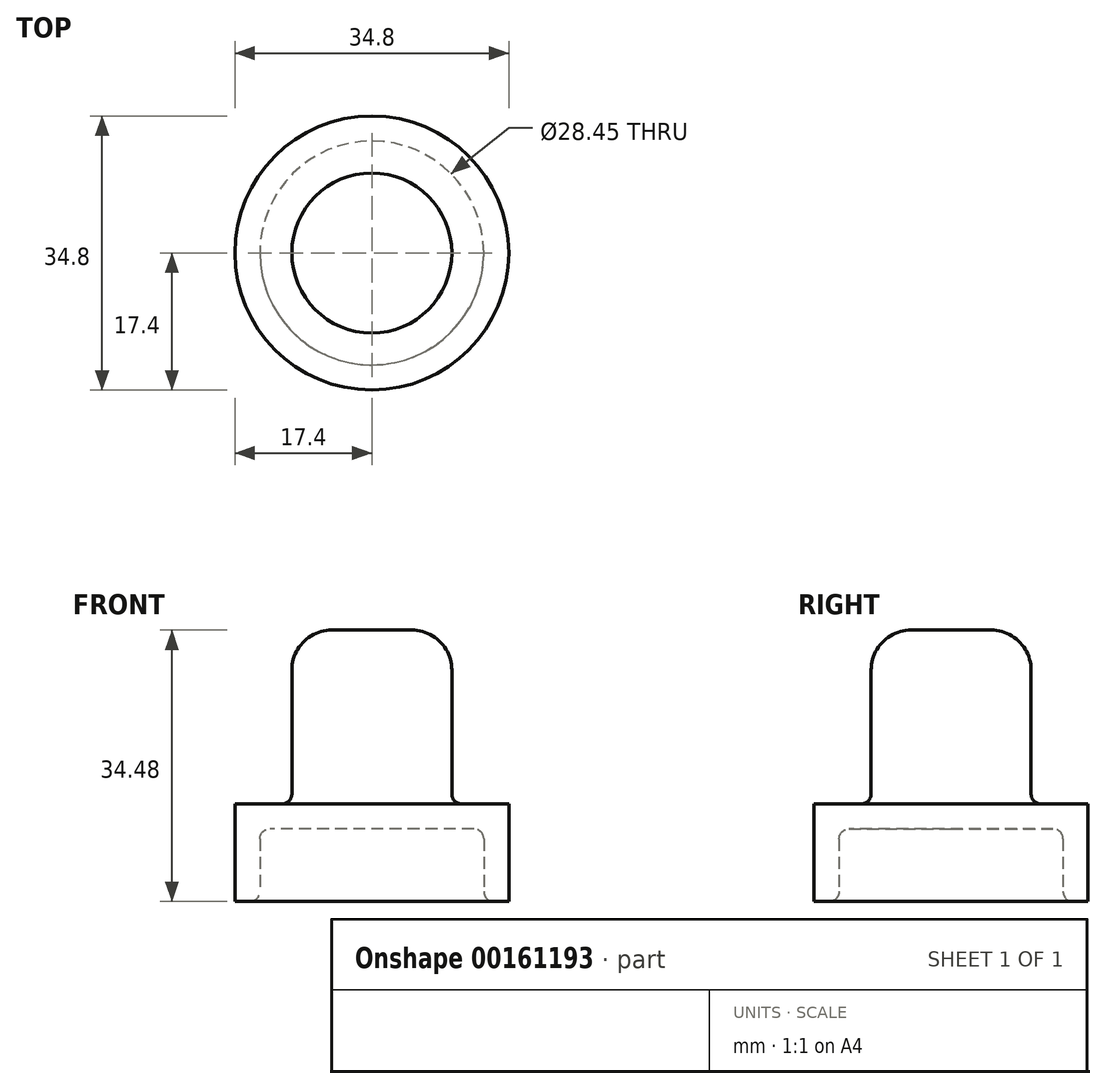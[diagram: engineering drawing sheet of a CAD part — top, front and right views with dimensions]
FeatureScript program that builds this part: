
annotation { "Feature Type Name" : "Feature", "Feature Type Description" : "" }
export const myFeature = defineFeature(function(context is Context, id is Id, definition is map)
    precondition{}
    {
        {
            var Q0;
            Q0=qCreatedBy(makeId("Front.planeOp"),FACE);
            var sketch = newSketch(context, id + "F0", { "sketchPlane" : qUnion([Q0])});
            skLineSegment(sketch, "E0", {"start": v(17.4, 0) * mm, "end": v(17.4, 12.4) * mm});
            skLineSegment(sketch, "E1", {"start": v(17.4, 12.4) * mm, "end": v(10.16, 12.4) * mm});
            skLineSegment(sketch, "E2", {"start": v(10.16, 12.4) * mm, "end": v(10.16, 34.48) * mm});
            skLineSegment(sketch, "E3", {"start": v(10.16, 34.48) * mm, "end": v(0, 34.48) * mm});
            skLineSegment(sketch, "E4", {"start": v(14.22, 0) * mm, "end": v(14.22, 9.22) * mm});
            skLineSegment(sketch, "E5", {"start": v(14.22, 9.22) * mm, "end": v(0, 9.22) * mm});
            skLineSegment(sketch, "E6", {"start": v(0, 9.22) * mm, "end": v(0, 34.48) * mm});
            skLineSegment(sketch, "E7", {"start": v(14.22, 0) * mm, "end": v(17.4, 0) * mm});
            skSolve(sketch);
        }
        {
            var Q0;
            Q0 = qSketchRegion(id + "F0", true);
            var Q1;
            Q1=sQuery(id+"F0.wireOp",EDGE,"E6");
            revolve(context, id + "F1", {"entities" : qUnion([Q0]), "axis" : qUnion([Q1]), "revolveType" : RevolveType.FULL});
        }
        {
            var Q0;
            Q0=makeQuery(id+"F1.opRevolve","SWEPT_EDGE",EDGE,{"disambiguationData":[OSD([sQuery(id+"F0.wireOp",EDGE,"E2"),sQuery(id+"F0.wireOp",EDGE,"E3")])]});
            fillet(context, id + "F2", {"entities" : qUnion([Q0]), "radius" : 5.08 * mm, "tangentPropagation" : true, "allowEdgeOverflow" : false});
        }
        {
            var Q0;
            Q0=makeQuery(id+"F1.opRevolve","SWEPT_EDGE",EDGE,{"disambiguationData":[OSD([sQuery(id+"F0.wireOp",EDGE,"E1"),sQuery(id+"F0.wireOp",EDGE,"E2")])]});
            fillet(context, id + "F3", {"entities" : qUnion([Q0]), "radius" : 1.27 * mm, "tangentPropagation" : true, "allowEdgeOverflow" : false});
        }
        {
            var Q0;
            Q0=makeQuery(id+"F1.opRevolve","SWEPT_EDGE",EDGE,{"disambiguationData":[OSD([sQuery(id+"F0.wireOp",EDGE,"E4"),sQuery(id+"F0.wireOp",EDGE,"E5")])]});
            var Q1;
            Q1=makeQuery(id+"F1.opRevolve","SWEPT_EDGE",EDGE,{"disambiguationData":[OSD([sQuery(id+"F0.wireOp",EDGE,"E4"),sQuery(id+"F0.wireOp",EDGE,"E7")])]});
            fillet(context, id + "F4", {"entities" : qUnion([Q0, Q1]), "radius" : 1.27 * mm, "tangentPropagation" : true, "allowEdgeOverflow" : false});
        }
    });
